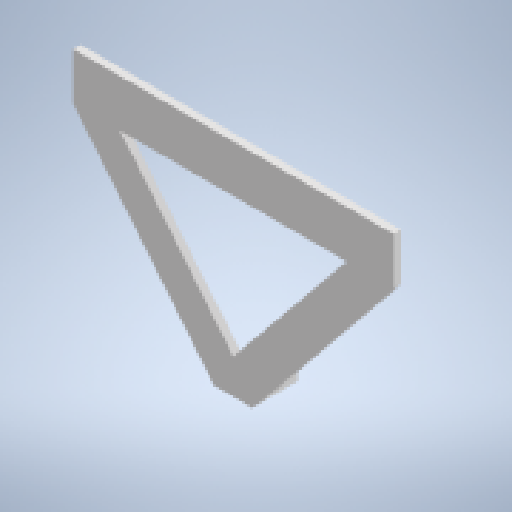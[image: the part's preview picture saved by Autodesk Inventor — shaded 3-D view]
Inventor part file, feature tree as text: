
AUTODESK INVENTOR PART (.ipt)
format: ipt  version: 2024 (Build 280153000, 153)  size: 207,360 bytes
history: native  units: in
note: dims shown in document units (in); Inventor stores cm internally (conversion verified against a paired STEP export)
features: extrude x4, sketch x2, chamfer x2
ambient origin geometry x8: Origin, YZ Plane, XZ Plane, XY Plane, X Axis, Y Axis, Z Axis, Center Point
bodies: Solid1 (feature_tree)
feature tree (8):
  sketch  "Sketch1"  dims[d0=1.1811in d1=1.5945in]
  extrude  "Extrusion1"  Depth=1.1811in
  extrude  "Extrusion2"  Depth=0.1969in
  extrude  "Extrusion3"  Depth=0.0787in
  chamfer  "Chamfer1"  Distance=0.1969in
  extrude  "Extrusion4"  Depth=0.1969in
  chamfer  "Chamfer2"  Distance=0.0236in
  sketch  "Sketch3"  dims[d4=0.1969in d5=0.1969in d7=0.0787in d8=0.1969in d9=0.0984in d10=0.0236in d11=0.0in d12=0.9055in d13=0.1969in d14=0.0in d15=0.1969in d16=0.2362in d17=0.0in d18=0.0984in d19=0.1969in d20=45.0deg d23=0.0394in d24=0.0394in d25=0.1181in d26=0.0in d27=0.0197in d28=0.1969in d29=45.0deg]
